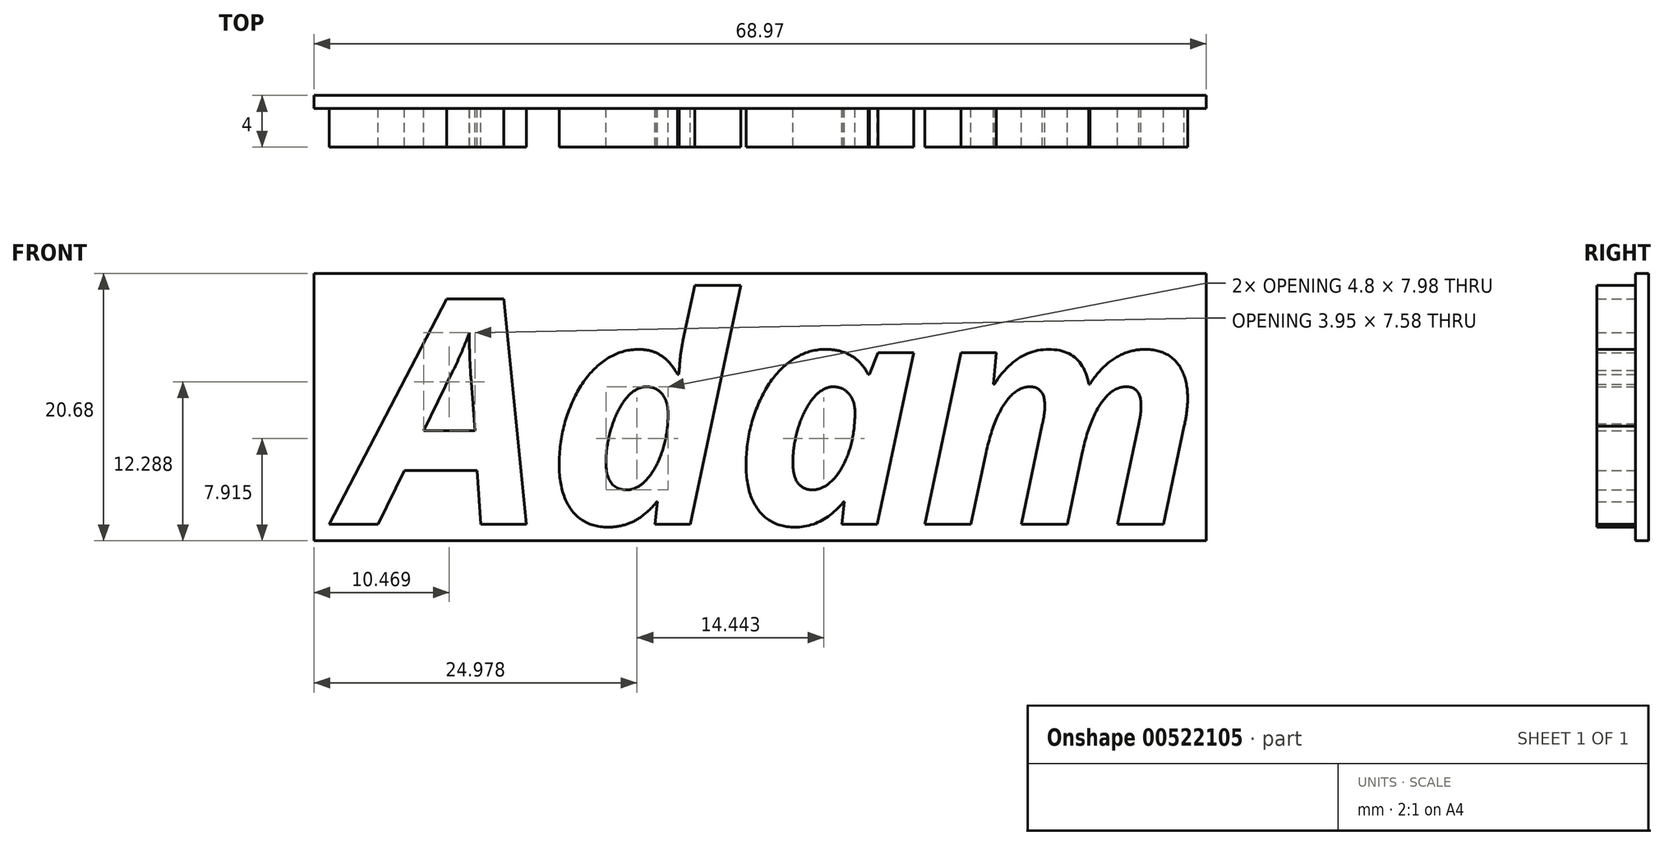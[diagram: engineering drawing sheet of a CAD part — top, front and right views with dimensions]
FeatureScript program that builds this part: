
annotation { "Feature Type Name" : "Feature", "Feature Type Description" : "" }
export const myFeature = defineFeature(function(context is Context, id is Id, definition is map)
    precondition{}
    {
        {
            var Q0;
            Q0=qCreatedBy(makeId("Front.planeOp"),FACE);
            var sketch = newSketch(context, id + "F0", { "sketchPlane" : qUnion([Q0])});
            skText(sketch, "E0", { "text": "Adam", "fontName": "OpenSans-BoldItalic.ttf"});
            const initialGuessF0  = {"E0": [-0.04475, -0.00012, 1, 0, 0.0175]};
            skSetInitialGuess(sketch, initialGuessF0);
            skSolve(sketch);
        }
        {
            var Q0;
            Q0=qSketchRegion(id+"F0",true);
            extrude(context, id + "F1", {"entities" : qUnion([Q0]), "depth" : 3 * mm});
        }
        {
            var Q0;
            Q0=makeQuery(id+"F0.imprint","IMPRINT",FACE,{"disambiguationData":[TD([[makeQuery(id+"F0.imprint","IMPRINT",EDGE,{"derivedFrom":sQuery(id+"F0.wireOp",EDGE,"E0.sketch_text.stroke-36")}),-1.0]])]});
            var sketch = newSketch(context, id + "F2", { "sketchPlane" : qUnion([Q0])});
            skLineSegment(sketch, "E1.bottom", {"start": v(-47.38, 19.28) * mm, "end": v(21.6, 19.28) * mm});
            skLineSegment(sketch, "E1.top", {"start": v(-47.38, -1.4) * mm, "end": v(21.6, -1.4) * mm});
            skLineSegment(sketch, "E1.left", {"start": v(-47.38, 19.28) * mm, "end": v(-47.38, -1.4) * mm});
            skLineSegment(sketch, "E1.right", {"start": v(21.6, 19.28) * mm, "end": v(21.6, -1.4) * mm});
            skSolve(sketch);
        }
        {
            var Q0;
            Q0=qSketchRegion(id+"F2",true);
            extrude(context, id + "F3", {"entities" : qUnion([Q0]), "oppositeDirection" : true, "depth" : 1 * mm, "offsetDistance" : 25 * mm});
        }
    });
